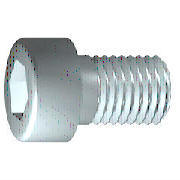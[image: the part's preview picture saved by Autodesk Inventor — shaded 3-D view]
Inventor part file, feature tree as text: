
AUTODESK INVENTOR PART (.ipt)
format: ipt  version: 2025.2 (Build 292293000, 293)  size: 200,192 bytes
history: native  units: mm (DEFAULTED — no unit token found)
features: other x1, extrude x1, chamfer x1, plane x1, fillet x1
ambient origin geometry x7: Origin, YZ Plane, XY Plane, X Axis, Y Axis, Z Axis, Center Point
bodies: Solid1 (feature_tree)
feature tree (5):
  other  "Körper"
  extrude  "Loch"  Depth=3.5mm
  chamfer  "Fase1"  Distance=0.306825mm
  plane  "Work Plane1"
  fillet  "Fillet2"  Radius=3.0mm
